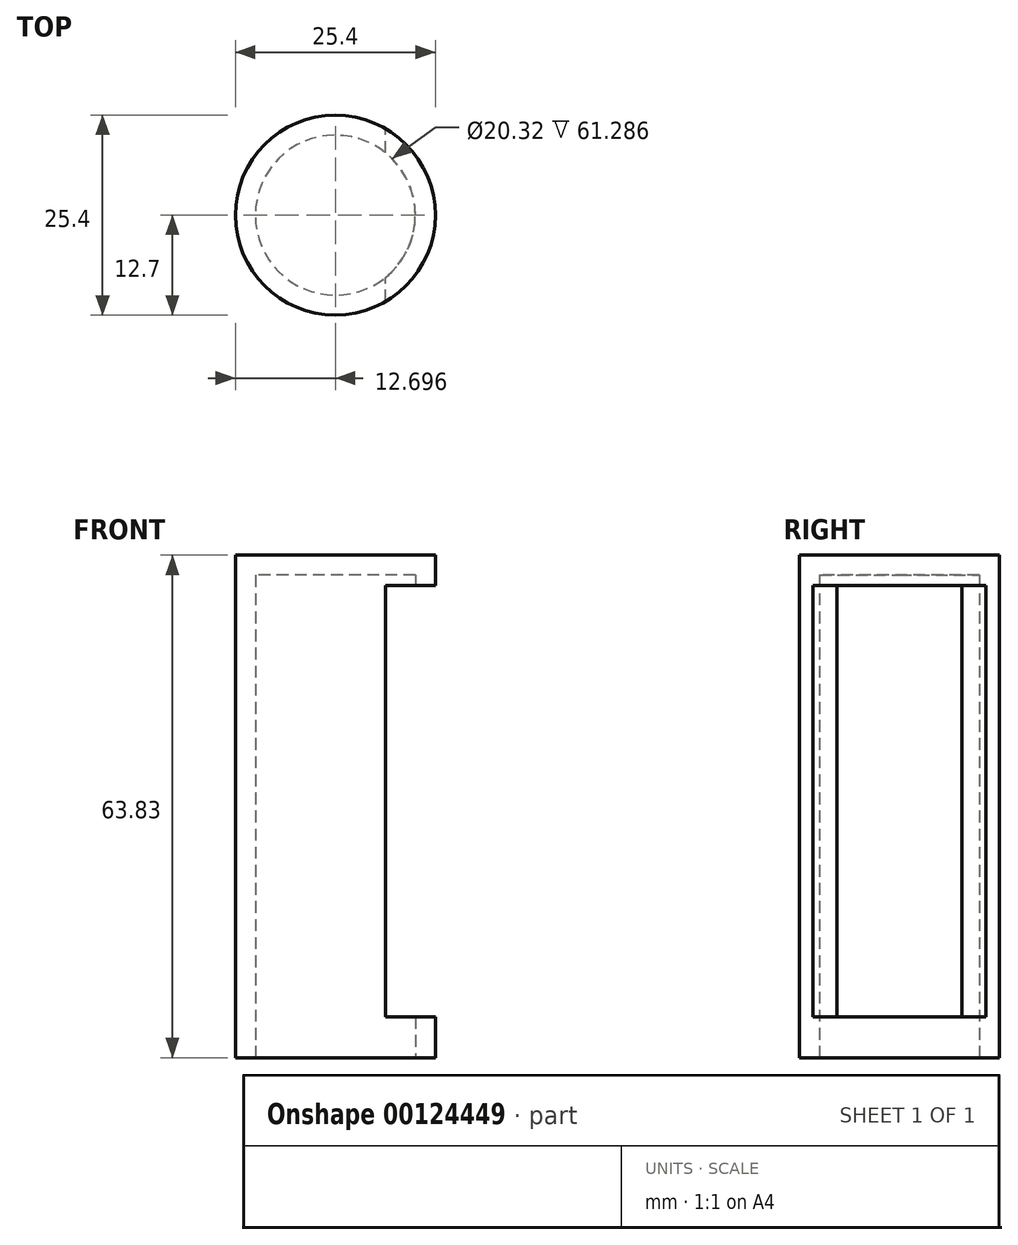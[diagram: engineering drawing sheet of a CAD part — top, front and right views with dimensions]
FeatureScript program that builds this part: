
annotation { "Feature Type Name" : "Feature", "Feature Type Description" : "" }
export const myFeature = defineFeature(function(context is Context, id is Id, definition is map)
    precondition{}
    {
        {
            var Q0;
            Q0=qCreatedBy(makeId("Top.planeOp"),FACE);
            var sketch = newSketch(context, id + "F0", { "sketchPlane" : qUnion([Q0])});
            skCircle(sketch, "E0", {"center": v(-51.78, 43.92) * mm, "radius": 12.7 * mm});
            skSolve(sketch);
        }
        {
            var Q0;
            Q0=makeQuery(id+"F0.imprint","IMPRINT",FACE,{"disambiguationData":[TD([[makeQuery(id+"F0.imprint","IMPRINT",EDGE,{"derivedFrom":sQuery(id+"F0.wireOp",EDGE,"E0")}),1.0]])]});
            extrude(context, id + "F1", {"entities" : qUnion([Q0]), "depth" : 63.83 * mm});
        }
        {
            var Q0;
            Q0=qCreatedBy(makeId("Front.planeOp"),FACE);
            var sketch = newSketch(context, id + "F2", { "sketchPlane" : qUnion([Q0])});
            skLineSegment(sketch, "E1.bottom", {"start": v(-32.97, 55) * mm, "end": v(-73.92, 55) * mm});
            skLineSegment(sketch, "E1.top", {"start": v(-32.97, 10.35) * mm, "end": v(-73.92, 10.35) * mm});
            skLineSegment(sketch, "E1.left", {"start": v(-32.97, 55) * mm, "end": v(-32.97, 10.35) * mm});
            skLineSegment(sketch, "E1.right", {"start": v(-73.92, 55) * mm, "end": v(-73.92, 10.35) * mm});
            skSolve(sketch);
        }
        {
            var Q0;
            Q0=makeQuery(id+"F1.opExtrude","CAP_FACE",FACE,{"disambiguationData":[OSD([sQuery(id+"F0.wireOp",EDGE,"E0")])],"isStart":true});
            shell(context, id + "F3", {"entities" : qUnion([Q0]), "thickness" : 2.54 * mm});
        }
        {
            var Q0;
            Q0=qCreatedBy(makeId("Right.planeOp"),FACE);
            var sketch = newSketch(context, id + "F4", { "sketchPlane" : qUnion([Q0])});
            skLineSegment(sketch, "E2.bottom", {"start": v(26.38, 5.17) * mm, "end": v(69.4, 5.17) * mm});
            skLineSegment(sketch, "E2.top", {"start": v(26.38, 59.98) * mm, "end": v(69.4, 59.98) * mm});
            skLineSegment(sketch, "E2.left", {"start": v(26.38, 5.17) * mm, "end": v(26.38, 59.98) * mm});
            skLineSegment(sketch, "E2.right", {"start": v(69.4, 5.17) * mm, "end": v(69.4, 59.98) * mm});
            skSolve(sketch);
        }
        {
            var Q0;
            Q0 = qSketchRegion(id + "F4", true);
            extrude(context, id + "F5", {"entities" : qUnion([Q0]), "operationType" : NewBodyOperationType.REMOVE, "oppositeDirection" : true, "depth" : 45.42 * mm});
        }
        {
            var Q0;
            Q0 = qSketchRegion(id + "F2", true);
            extrude(context, id + "F6", {"entities" : qUnion([Q0]), "operationType" : NewBodyOperationType.REMOVE, "oppositeDirection" : true, "depth" : 29.86 * mm});
        }
    });
